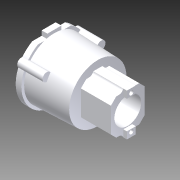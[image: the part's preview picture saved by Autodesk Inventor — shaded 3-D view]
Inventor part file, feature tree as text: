
AUTODESK INVENTOR PART (.ipt)
format: ipt  version: 2012 (Build 160160000, 160)  size: 244,224 bytes
history: native  units: in
note: dims shown in document units (in); Inventor stores cm internally (conversion verified against a paired STEP export)
features: extrude x9, sketch x5, revolve x1, fillet x1, chamfer x1, projected_geometry x1
ambient origin geometry x8: Origin, YZ Plane, XZ Plane, XY Plane, X Axis, Y Axis, Z Axis, Center Point
bodies: Solid1 (feature_tree)
feature tree (18):
  revolve  "Revolution1"  [1 undecoded]
  sketch  "Sketch2"  dims[d2=0.9225in d3=1.375in]
  extrude  "Extrusion1"  Depth=1.375in
  extrude  "Extrusion2"  TaperAngle=90.0deg  [1 undecoded]
  extrude  "Extrusion3"  Depth=0.24in
  extrude  "Extrusion4"  Depth=0.24in
  sketch  "Sketch3"  dims[d4=0.802in d5=90.0deg]
  extrude  "Extrusion5"  Depth=1.523in
  extrude  "Extrusion6"  Depth=1.523in
  extrude  "Extrusion7"  Depth=1.524in
  sketch  "Sketch5"  dims[d8=0.24in d9=0.24in d10=1.523in d11=1.523in d12=1.524in d15=0.0in d16=0.8in d17=0.392in d18=0.196in d19=0.132in d20=0.71in d21=0.0in d22=0.5in d23=0.0in d24=0.16in d25=0.0in d26=0.16in d27=0.0in d28=1.0in d29=0.945in d30=0.5in d31=0.4725in d32=0.0925in d33=0.25in d34=0.125in d35=0.0925in d36=0.94in d37=0.0in d38=0.84in d39=0.0in d40=0.75in d41=0.84in d42=0.0in d43=0.472in d44=0.472in d52=0.197in d53=0.197in d54=0.84in d55=0.0in d56=0.116in d57=0.116in d58=0.84in d59=0.0in d60=0.125in d61=0.15in d62=0.125in d63=45.0deg]
  extrude  "Extrusion8"  TaperAngle=0.0deg  [1 undecoded]
  extrude  "Extrusion9"  Depth=0.8in
  fillet  "Fillet1"  Radius=0.392in
  chamfer  "Chamfer1"  Distance=0.196in
  sketch  "Sketch1"  dims[d0=0.16in d1=0.075in]
  sketch  "Sketch4"  dims[d6=1.759in d7=0.24in]
  projected_geometry  "Projected Loop1"
note: 3 required parameter values undecoded (feature->parameter linkage not recoverable at this tier; creation-order binding heuristic only, values carry confidence <= 0.55)